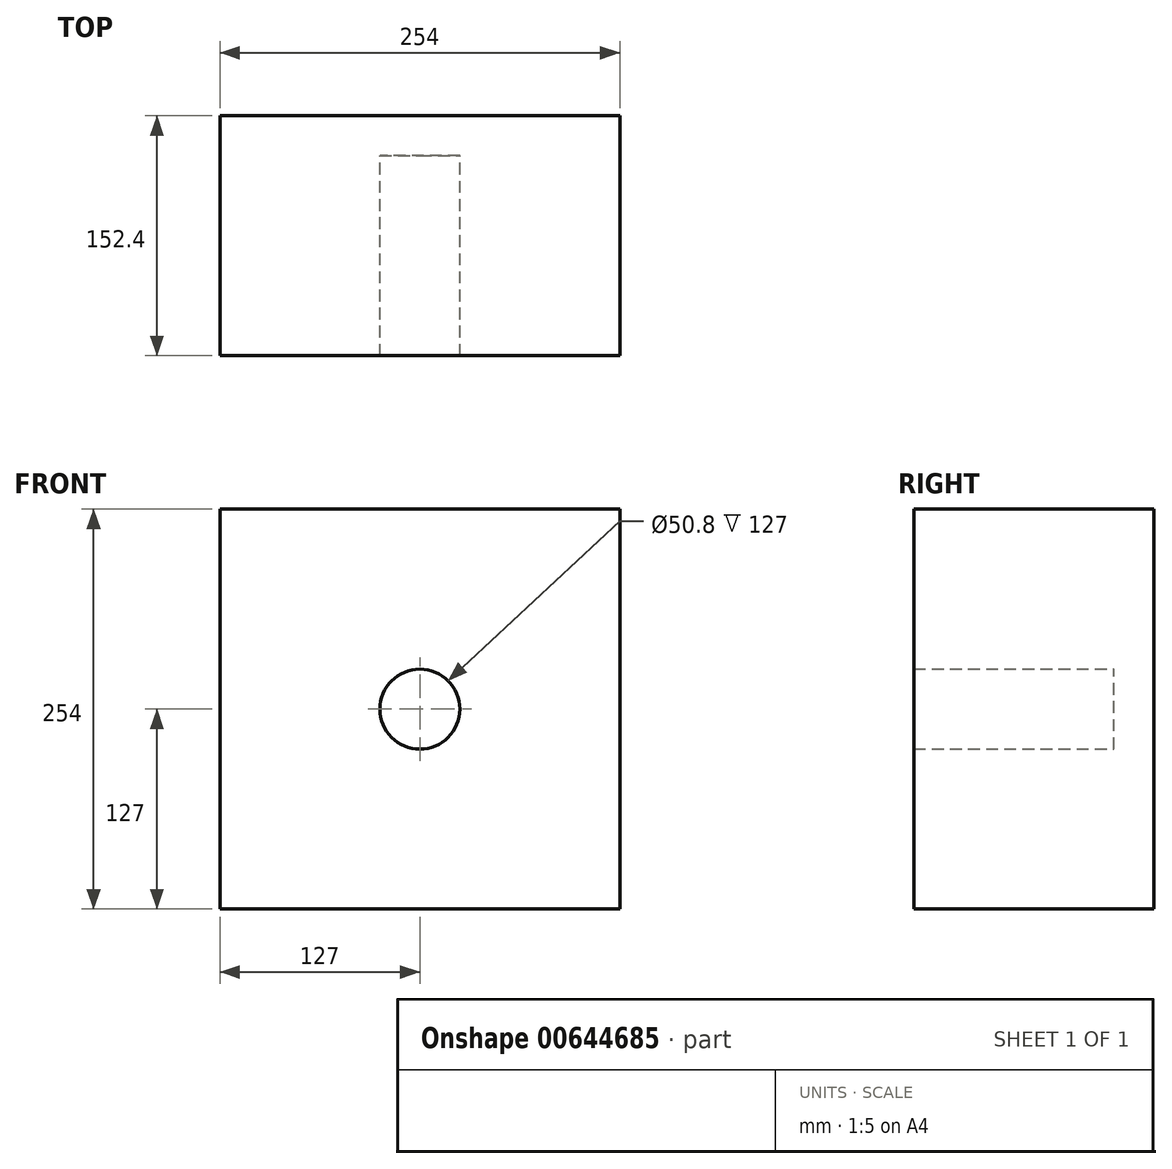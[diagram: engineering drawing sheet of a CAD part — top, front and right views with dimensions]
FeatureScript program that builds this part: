
annotation { "Feature Type Name" : "Feature", "Feature Type Description" : "" }
export const myFeature = defineFeature(function(context is Context, id is Id, definition is map)
    precondition{}
    {
        {
            var Q0;
            Q0=qCreatedBy(makeId("Front.planeOp"),FACE);
            var sketch = newSketch(context, id + "F0", { "sketchPlane" : qUnion([Q0])});
            skLineSegment(sketch, "E0.bottom", {"start": v(-127, 127) * mm, "end": v(127, 127) * mm});
            skLineSegment(sketch, "E0.top", {"start": v(-127, -127) * mm, "end": v(127, -127) * mm});
            skLineSegment(sketch, "E0.left", {"start": v(-127, 127) * mm, "end": v(-127, -127) * mm});
            skLineSegment(sketch, "E0.right", {"start": v(127, 127) * mm, "end": v(127, -127) * mm});
            skPoint(sketch, "E0.middle", {"position": v(0, 0) * mm});
            skCircle(sketch, "E1", {"center": v(0, 0) * mm, "radius": 25.4 * mm});
            skSolve(sketch);
        }
        {
            var Q0;
            Q0=makeQuery(id+"F0.imprint","IMPRINT",FACE,{"disambiguationData":[TD([[makeQuery(id+"F0.imprint","IMPRINT",EDGE,{"derivedFrom":sQuery(id+"F0.wireOp",EDGE,"E0.bottom")}),-1.0]])]});
            extrude(context, id + "F1", {"entities" : qUnion([Q0]), "depth" : 127 * mm, "offsetDistance" : 25.4 * mm});
        }
        {
            var Q0;
            Q0=makeQuery(id+"F1.opExtrude","CAP_FACE",FACE,{"disambiguationData":[OSD([sQuery(id+"F0.wireOp",EDGE,"E0.bottom"),sQuery(id+"F0.wireOp",EDGE,"E0.top"),sQuery(id+"F0.wireOp",EDGE,"E0.left"),sQuery(id+"F0.wireOp",EDGE,"E0.right"),sQuery(id+"F0.wireOp",EDGE,"E1")])],"isStart":true});
            var sketch = newSketch(context, id + "F2", { "sketchPlane" : qUnion([Q0])});
            skLineSegment(sketch, "E2.bottom", {"start": v(-127, -127) * mm, "end": v(127, -127) * mm});
            skLineSegment(sketch, "E2.top", {"start": v(-127, 127) * mm, "end": v(127, 127) * mm});
            skLineSegment(sketch, "E2.left", {"start": v(-127, -127) * mm, "end": v(-127, 127) * mm});
            skLineSegment(sketch, "E2.right", {"start": v(127, -127) * mm, "end": v(127, 127) * mm});
            skSolve(sketch);
        }
        {
            var Q0;
            Q0 = qSketchRegion(id + "F2", true);
            extrude(context, id + "F3", {"entities" : qUnion([Q0]), "operationType" : NewBodyOperationType.ADD, "depth" : 25.4 * mm, "offsetDistance" : 25.4 * mm});
        }
    });
